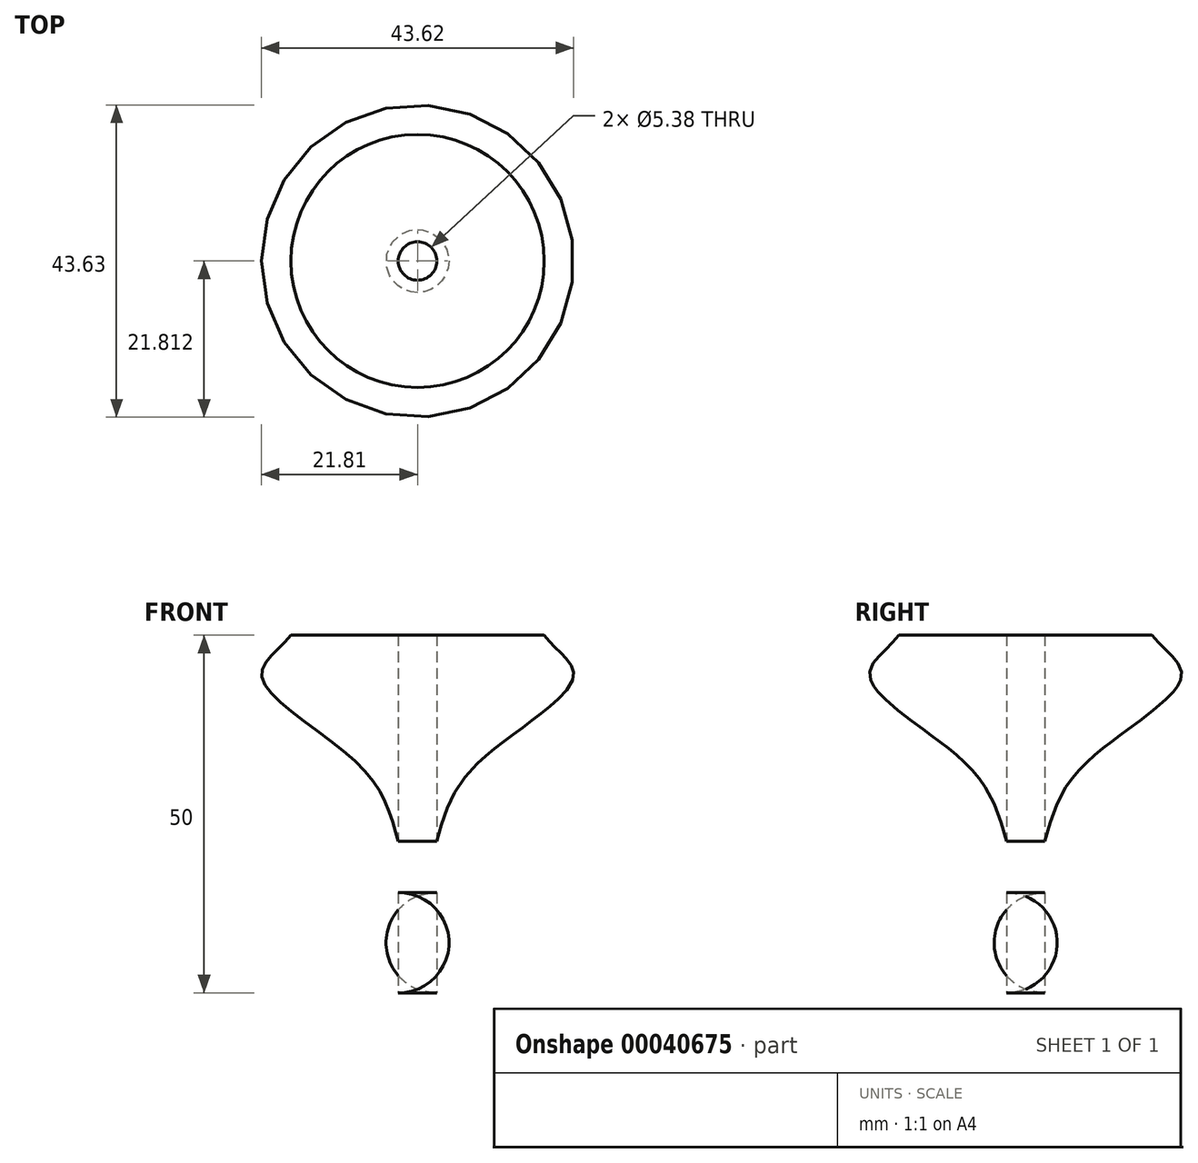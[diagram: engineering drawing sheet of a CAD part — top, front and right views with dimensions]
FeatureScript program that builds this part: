
annotation { "Feature Type Name" : "Feature", "Feature Type Description" : "" }
export const myFeature = defineFeature(function(context is Context, id is Id, definition is map)
    precondition{}
    {
        {
            var Q0;
            Q0=qCreatedBy(makeId("Right.planeOp"),FACE);
            var sketch = newSketch(context, id + "F0", { "sketchPlane" : qUnion([Q0])});
            skArc(sketch, "E0", {"start": v(0, -36.98) * mm, "mid": v(6.91, -29.98) * mm, "end": v(0, -22.98) * mm});
            skFitSpline(sketch, "E1", {"points": [v(0, -22.98) * mm, v(10.15, -19.86) * mm, v(0, -16.27) * mm, v(0, -15.98) * mm], "startDerivative": vector(36.99, 6.06) * mm, "endDerivative": vector(2.64, 3.54) * mm});
            skFitSpline(sketch, "E2", {"points": [v(-0.07, -16.07) * mm, v(5.38, -5.23) * mm, v(19.11, 7.32) * mm, v(15, 13.02) * mm], "startDerivative": vector(8.79, 31.9) * mm, "endDerivative": vector(-16.38, 22.74) * mm});
            skLineSegment(sketch, "E3", {"start": v(15, 13.02) * mm, "end": v(0, 13.02) * mm});
            skLineSegment(sketch, "E4", {"start": v(0, -36.98) * mm, "end": v(0, 13.02) * mm});
            skLineSegment(sketch, "E5", {"start": v(-2.69, -37.18) * mm, "end": v(-2.69, 12.82) * mm});
            skSolve(sketch);
        }
        {
            var Q0;
            {var subQ3=sQuery(id+"F0.wireOp",EDGE,"E3");Q0=makeQuery(id+"F0.imprint","IMPRINT",FACE,{"disambiguationData":[TD([[makeQuery(id+"F0.imprint","IMPRINT",EDGE,{"derivedFrom":subQ3}),1.0]])]});}
            var Q1;
            {var subQ0=sQuery(id+"F0.wireOp",EDGE,"E4");var subQ1=sQuery(id+"F0.wireOp",EDGE,"E1");var subQ2=makeQuery(id+"F0.imprint","INTERSECT",VERTEX,{"disambiguationData":[OD(1.0)],"derivedFrom":[subQ1,subQ0]});Q1=makeQuery(id+"F0.imprint","IMPRINT",FACE,{"disambiguationData":[TD([[makeQuery(id+"F0.imprint","IMPRINT",EDGE,{"disambiguationData":[TD([[subQ2,1.0]])],"derivedFrom":subQ1}),1.0]])]});}
            var Q2;
            {var subQ1=sQuery(id+"F0.wireOp",EDGE,"E0");Q2=makeQuery(id+"F0.imprint","IMPRINT",FACE,{"disambiguationData":[TD([[makeQuery(id+"F0.imprint","IMPRINT",EDGE,{"derivedFrom":subQ1}),1.0]])]});}
            var Q3;
            Q3=sQuery(id+"F0.wireOp",EDGE,"E5");
            revolve(context, id + "F1", {"entities" : qUnion([Q0, Q1, Q2]), "axis" : qUnion([Q3]), "revolveType" : RevolveType.FULL});
        }
    });
